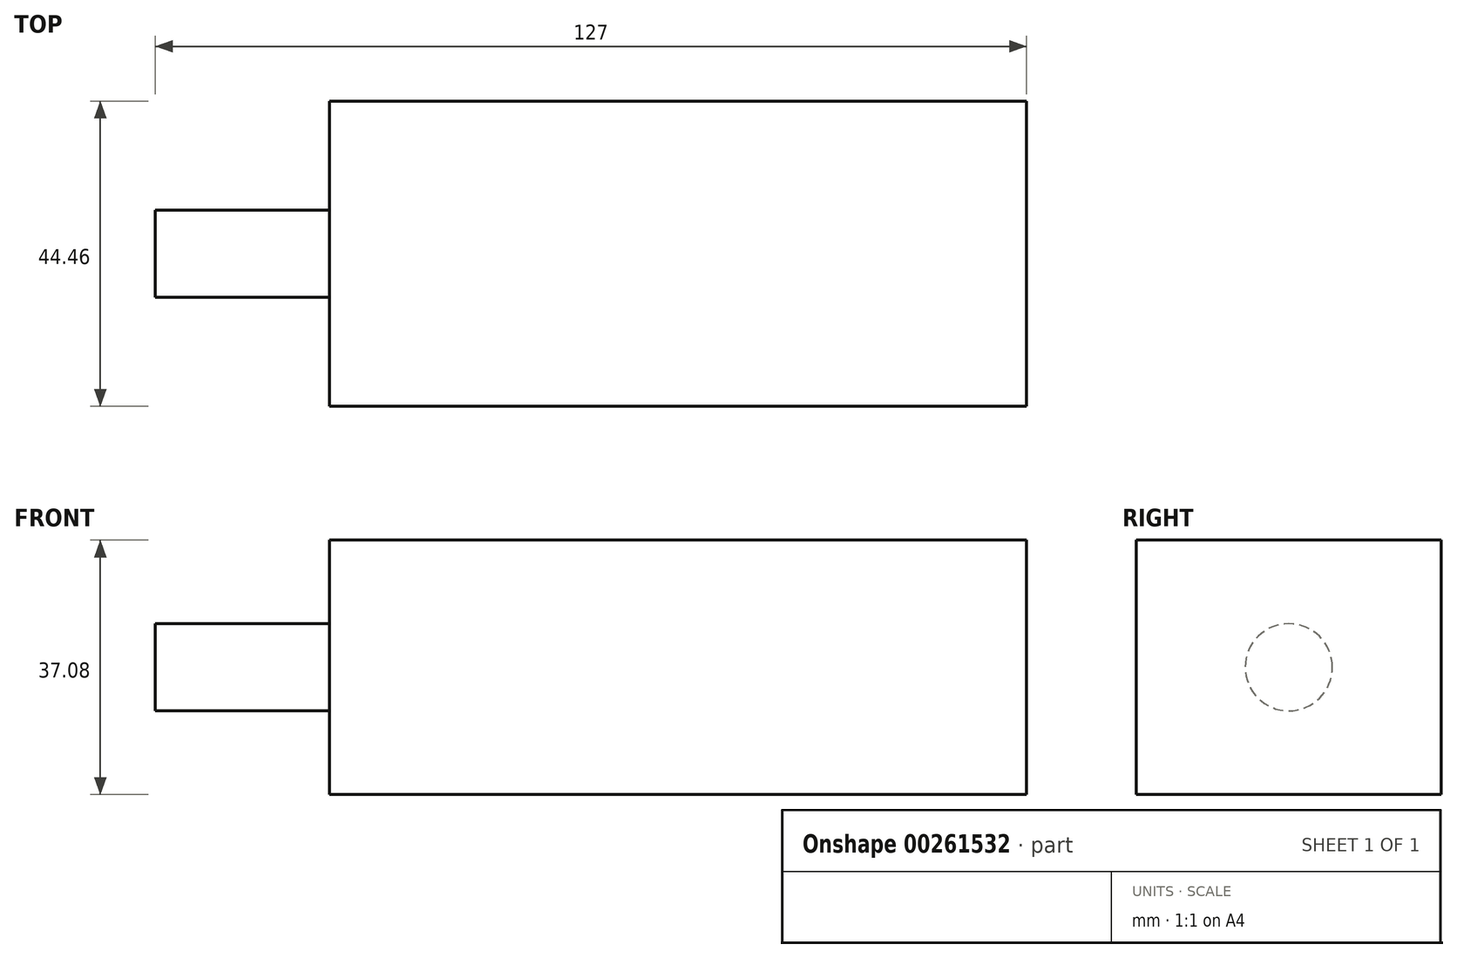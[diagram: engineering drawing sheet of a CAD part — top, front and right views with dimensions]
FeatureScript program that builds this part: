
annotation { "Feature Type Name" : "Feature", "Feature Type Description" : "" }
export const myFeature = defineFeature(function(context is Context, id is Id, definition is map)
    precondition{}
    {
        {
            var Q0;
            Q0=qCreatedBy(makeId("Top.planeOp"),FACE);
            var sketch = newSketch(context, id + "F0", { "sketchPlane" : qUnion([Q0])});
            skLineSegment(sketch, "E0.bottom", {"start": v(-50.8, 22.22) * mm, "end": v(50.8, 22.22) * mm});
            skLineSegment(sketch, "E0.top", {"start": v(-50.8, -22.23) * mm, "end": v(50.8, -22.23) * mm});
            skLineSegment(sketch, "E0.left", {"start": v(-50.8, 22.22) * mm, "end": v(-50.8, -22.23) * mm});
            skLineSegment(sketch, "E0.right", {"start": v(50.8, 22.22) * mm, "end": v(50.8, -22.23) * mm});
            skPoint(sketch, "E0.middle", {"position": v(0, 0) * mm});
            skSolve(sketch);
        }
        {
            var Q0;
            Q0=makeQuery(id+"F0.imprint","IMPRINT",FACE,{"disambiguationData":[TD([[makeQuery(id+"F0.imprint","IMPRINT",EDGE,{"derivedFrom":sQuery(id+"F0.wireOp",EDGE,"E0.bottom")}),-1.0]])]});
            extrude(context, id + "F1", {"entities" : qUnion([Q0]), "depth" : 37.08 * mm});
        }
        {
            var Q0;
            Q0=makeQuery(id+"F1.opExtrude","SWEPT_FACE",FACE,{"disambiguationData":[OSD([sQuery(id+"F0.wireOp",EDGE,"E0.right")])]});
            var sketch = newSketch(context, id + "F2", { "sketchPlane" : qUnion([Q0])});
            skCircle(sketch, "E1", {"center": v(0, 18.54) * mm, "radius": 6.35 * mm});
            skSolve(sketch);
        }
        {
            var Q0;
            Q0=makeQuery(id+"F2.imprint","IMPRINT",FACE,{"disambiguationData":[TD([[makeQuery(id+"F2.imprint","IMPRINT",EDGE,{"derivedFrom":sQuery(id+"F2.wireOp",EDGE,"E1")}),1.0]])]});
            extrude(context, id + "F3", {"entities" : qUnion([Q0]), "operationType" : NewBodyOperationType.ADD, "oppositeDirection" : true, "depth" : 127 * mm});
        }
    });
